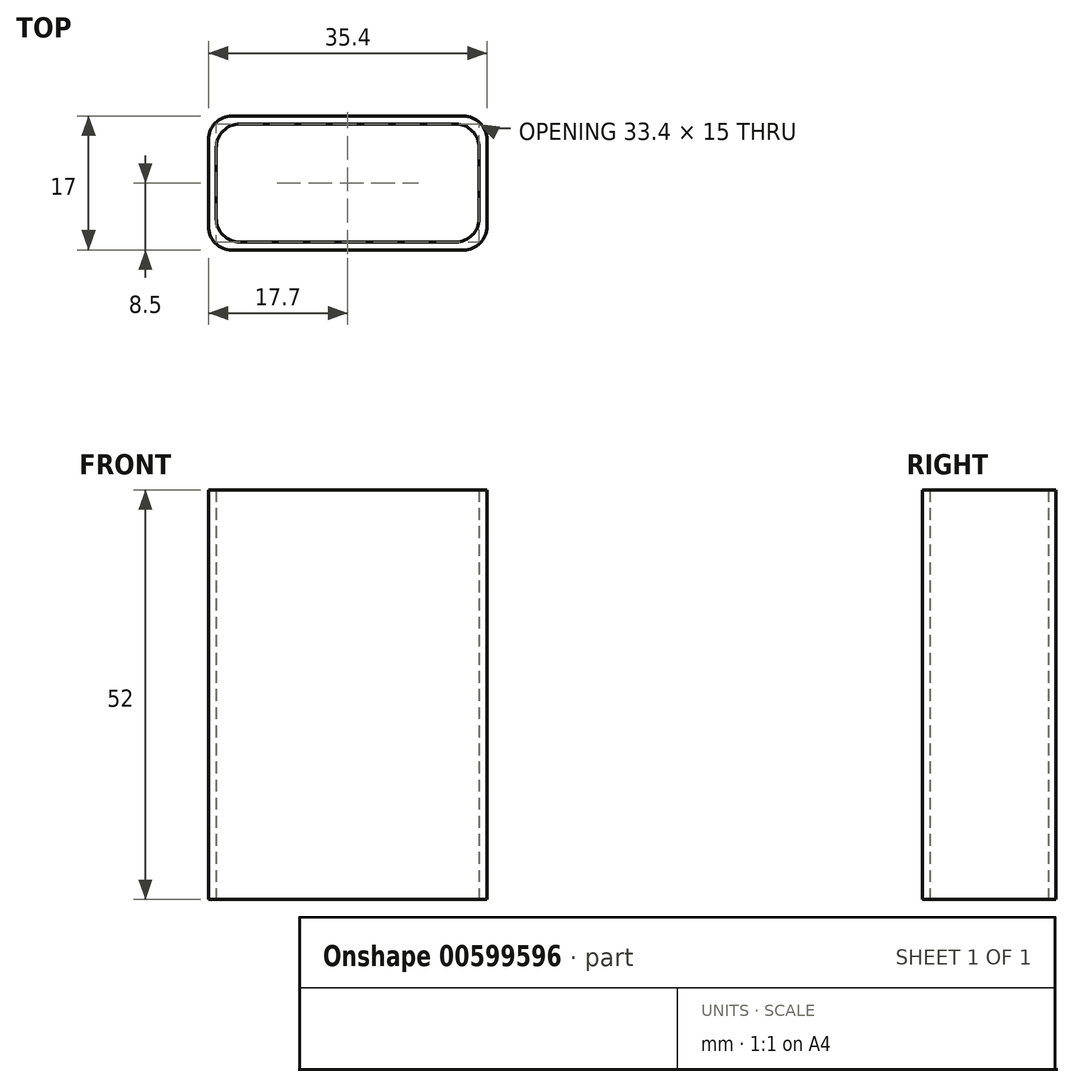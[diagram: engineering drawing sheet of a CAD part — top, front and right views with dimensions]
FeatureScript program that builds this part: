
annotation { "Feature Type Name" : "Feature", "Feature Type Description" : "" }
export const myFeature = defineFeature(function(context is Context, id is Id, definition is map)
    precondition{}
    {
        {
            var Q0;
            Q0=qCreatedBy(makeId("Top.planeOp"),FACE);
            var sketch = newSketch(context, id + "F0", { "sketchPlane" : qUnion([Q0])});
            skLineSegment(sketch, "E0.bottom", {"start": v(14.7, -8.5) * mm, "end": v(-14.7, -8.5) * mm});
            skLineSegment(sketch, "E0.top", {"start": v(14.7, 8.5) * mm, "end": v(-14.7, 8.5) * mm});
            skLineSegment(sketch, "E0.left", {"start": v(17.7, -5.5) * mm, "end": v(17.7, 5.5) * mm});
            skLineSegment(sketch, "E0.right", {"start": v(-17.7, -5.5) * mm, "end": v(-17.7, 5.5) * mm});
            skPoint(sketch, "E0.middle", {"position": v(0, 0) * mm});
            skLineSegment(sketch, "E1.0", {"start": v(13.7, 7.5) * mm, "end": v(-13.7, 7.5) * mm});
            skLineSegment(sketch, "E2.0", {"start": v(16.7, -4.5) * mm, "end": v(16.7, 4.5) * mm});
            skLineSegment(sketch, "E3.0", {"start": v(13.7, -7.5) * mm, "end": v(-13.7, -7.5) * mm});
            skLineSegment(sketch, "E4.0", {"start": v(-16.7, -4.5) * mm, "end": v(-16.7, 4.5) * mm});
            skPoint(sketch, "E5.visualSharp", {"position": v(-16.7, 7.5) * mm});
            skArc(sketch, "E5.filletArc", {"start": v(-13.7, 7.5) * mm, "mid": v(-15.82, 6.62) * mm, "end": v(-16.7, 4.5) * mm});
            skPoint(sketch, "E6.visualSharp", {"position": v(-17.7, 8.5) * mm});
            skArc(sketch, "E6.filletArc", {"start": v(-14.7, 8.5) * mm, "mid": v(-16.82, 7.62) * mm, "end": v(-17.7, 5.5) * mm});
            skPoint(sketch, "E7.visualSharp", {"position": v(16.7, 7.5) * mm});
            skArc(sketch, "E7.filletArc", {"start": v(16.7, 4.5) * mm, "mid": v(15.82, 6.62) * mm, "end": v(13.7, 7.5) * mm});
            skPoint(sketch, "E8.visualSharp", {"position": v(17.7, 8.5) * mm});
            skArc(sketch, "E8.filletArc", {"start": v(17.7, 5.5) * mm, "mid": v(16.82, 7.62) * mm, "end": v(14.7, 8.5) * mm});
            skPoint(sketch, "E9.visualSharp", {"position": v(16.7, -7.5) * mm});
            skArc(sketch, "E9.filletArc", {"start": v(13.7, -7.5) * mm, "mid": v(15.82, -6.62) * mm, "end": v(16.7, -4.5) * mm});
            skPoint(sketch, "E10.visualSharp", {"position": v(17.7, -8.5) * mm});
            skArc(sketch, "E10.filletArc", {"start": v(14.7, -8.5) * mm, "mid": v(16.82, -7.62) * mm, "end": v(17.7, -5.5) * mm});
            skPoint(sketch, "E11.visualSharp", {"position": v(-17.7, -8.5) * mm});
            skArc(sketch, "E11.filletArc", {"start": v(-17.7, -5.5) * mm, "mid": v(-16.82, -7.62) * mm, "end": v(-14.7, -8.5) * mm});
            skPoint(sketch, "E12.visualSharp", {"position": v(-16.7, -7.5) * mm});
            skArc(sketch, "E12.filletArc", {"start": v(-16.7, -4.5) * mm, "mid": v(-15.82, -6.62) * mm, "end": v(-13.7, -7.5) * mm});
            skSolve(sketch);
        }
        {
            var Q0;
            Q0=makeQuery(id+"F0.imprint","IMPRINT",FACE,{"disambiguationData":[TD([[makeQuery(id+"F0.imprint","IMPRINT",EDGE,{"derivedFrom":sQuery(id+"F0.wireOp",EDGE,"E0.bottom")}),-1.0]])]});
            extrude(context, id + "F1", {"entities" : qUnion([Q0]), "depth" : 52 * mm, "offsetDistance" : 25 * mm});
        }
        {
            var Q0;
            {var subQ0=sQuery(id+"F0.wireOp",EDGE,"E12.filletArc");var subQ1=sQuery(id+"F0.wireOp",EDGE,"E9.filletArc");var subQ2=sQuery(id+"F0.wireOp",EDGE,"E7.filletArc");var subQ3=sQuery(id+"F0.wireOp",EDGE,"E5.filletArc");var subQ4=sQuery(id+"F0.wireOp",EDGE,"E4.0");var subQ5=sQuery(id+"F0.wireOp",EDGE,"E3.0");var subQ6=sQuery(id+"F0.wireOp",EDGE,"E2.0");var subQ7=sQuery(id+"F0.wireOp",EDGE,"E1.0");Q0=makeQuery(id+"FoRdDZvHGKNCmAY_0.boolean.opBoolean","MERGE",FACE,{"derivedFrom":[makeQuery(id+"F1.opExtrude","CAP_FACE",FACE,{"disambiguationData":[OSD([sQuery(id+"F0.wireOp",EDGE,"E0.bottom"),sQuery(id+"F0.wireOp",EDGE,"E0.top"),sQuery(id+"F0.wireOp",EDGE,"E0.left"),sQuery(id+"F0.wireOp",EDGE,"E0.right"),subQ7,subQ6,subQ5,subQ4,subQ3,sQuery(id+"F0.wireOp",EDGE,"E6.filletArc"),subQ2,sQuery(id+"F0.wireOp",EDGE,"E8.filletArc"),subQ1,sQuery(id+"F0.wireOp",EDGE,"E10.filletArc"),sQuery(id+"F0.wireOp",EDGE,"E11.filletArc"),subQ0])],"isStart":true}),makeQuery(id+"FoRdDZvHGKNCmAY_0.opExtrude","CAP_FACE",FACE,{"disambiguationData":[OSD([subQ7,subQ6,subQ5,subQ4,subQ3,subQ2,subQ1,subQ0])],"isStart":true})]});}
            var sketch = newSketch(context, id + "F2", { "sketchPlane" : qUnion([Q0])});
            skLineSegment(sketch, "E13.bottom", {"start": v(-0.3, 2) * mm, "end": v(4.7, 2) * mm});
            skLineSegment(sketch, "E13.top", {"start": v(-0.3, -2) * mm, "end": v(4.7, -2) * mm});
            skLineSegment(sketch, "E13.left", {"start": v(-0.3, 2) * mm, "end": v(-0.3, -2) * mm});
            skLineSegment(sketch, "E13.right", {"start": v(4.7, 2) * mm, "end": v(4.7, -2) * mm});
            skSolve(sketch);
        }
        {
            var Q0;
            Q0=makeQuery(id+"F2.imprint","IMPRINT",FACE,{"disambiguationData":[TD([[makeQuery(id+"F2.imprint","IMPRINT",EDGE,{"derivedFrom":sQuery(id+"F2.wireOp",EDGE,"E13.bottom")}),-1.0]])]});
            extrude(context, id + "F3", {"entities" : qUnion([Q0]), "operationType" : NewBodyOperationType.REMOVE, "endBound" : BoundingType.THROUGH_ALL, "oppositeDirection" : true, "depth" : 25 * mm, "offsetDistance" : 25 * mm});
        }
    });
